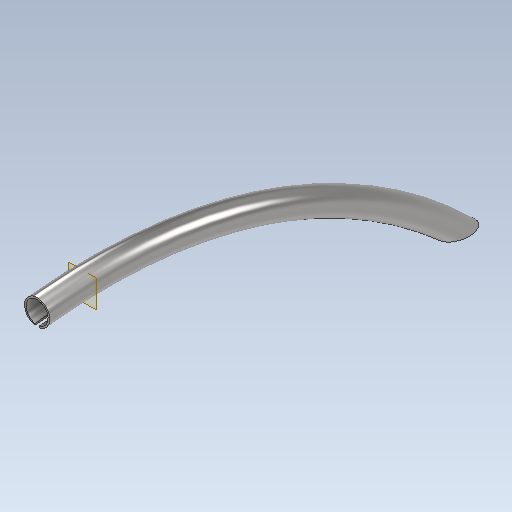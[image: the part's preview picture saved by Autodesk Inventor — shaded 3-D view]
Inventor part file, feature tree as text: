
AUTODESK INVENTOR PART (.ipt)
format: ipt  version: 2021 (Build 250183000, 183)  size: 231,424 bytes
history: native  units: mm
features: sketch x4, sweep x2, extrude x2, plane x1, split x1
ambient origin geometry x8: Origin, YZ Plane, XZ Plane, XY Plane, X Axis, Y Axis, Z Axis, Center Point
bodies: Solid1 (feature_tree)
feature tree (10):
  sketch  "Sketch1"  dims[d0=3300.0mm d1=1650.0mm]
  sweep  "Sweep1"
  sweep  "Sweep2"
  extrude  "Extrusion1"  Depth=70.0mm
  extrude  "Extrusion3"  Depth=1650.0mm
  plane  "Work Plane1"
  split  "Split1"
  sketch  "Sketch2"  dims[d2=0.0mm d3=80.0mm]
  sketch  "Sketch3"  dims[d4=0.0mm d5=0.0mm d6=70.0mm]
  sketch  "Sketch4"  dims[d7=0.0mm d8=1650.0mm d9=0.0mm d10=0.0mm d11=1810.0mm d12=3460.0mm d13=1730.0mm d14=1200.0mm d15=1730.0mm d16=1730.0mm d17=200.0mm d18=80.0mm d19=0.0mm d22=14.0mm d23=0.0mm d24=-144.0mm]
